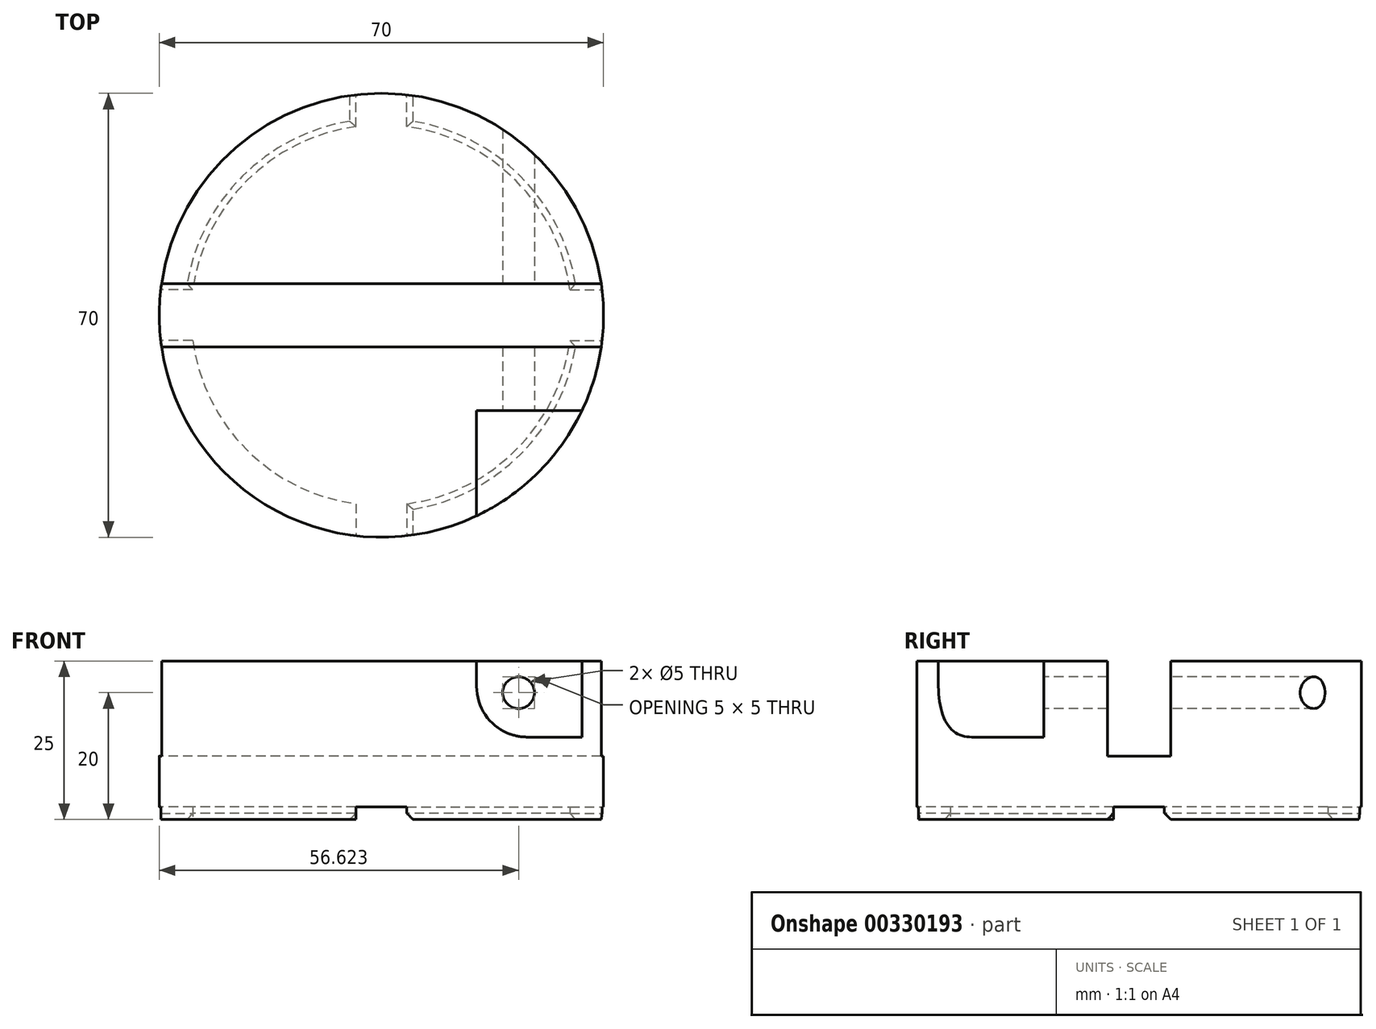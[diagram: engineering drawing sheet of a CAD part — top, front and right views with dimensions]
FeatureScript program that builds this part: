
annotation { "Feature Type Name" : "Feature", "Feature Type Description" : "" }
export const myFeature = defineFeature(function(context is Context, id is Id, definition is map)
    precondition{}
    {
        {
            var Q0;
            Q0=qCreatedBy(makeId("Top.planeOp"),FACE);
            var sketch = newSketch(context, id + "F0", { "sketchPlane" : qUnion([Q0])});
            skCircle(sketch, "E0", {"center": v(0, 0) * mm, "radius": 35 * mm});
            skSolve(sketch);
        }
        {
            var Q0;
            Q0=makeQuery(id+"F0.imprint","IMPRINT",FACE,{"disambiguationData":[TD([[makeQuery(id+"F0.imprint","IMPRINT",EDGE,{"derivedFrom":sQuery(id+"F0.wireOp",EDGE,"E0")}),1.0]])]});
            extrude(context, id + "F1", {"entities" : qUnion([Q0]), "depth" : 25 * mm});
        }
        {
            var Q0;
            Q0=makeQuery(id+"F1.opExtrude","CAP_FACE",FACE,{"disambiguationData":[OSD([sQuery(id+"F0.wireOp",EDGE,"E0")])],"isStart":false});
            var sketch = newSketch(context, id + "F2", { "sketchPlane" : qUnion([Q0])});
            skLineSegment(sketch, "E1.bottom", {"start": v(35, 5) * mm, "end": v(-35, 5) * mm});
            skLineSegment(sketch, "E1.top", {"start": v(35, -5) * mm, "end": v(-35, -5) * mm});
            skLineSegment(sketch, "E1.left", {"start": v(35, 5) * mm, "end": v(35, -5) * mm});
            skLineSegment(sketch, "E1.right", {"start": v(-35, 5) * mm, "end": v(-35, -5) * mm});
            skPoint(sketch, "E1.middle", {"position": v(0, 0) * mm});
            skSolve(sketch);
        }
        {
            var Q0;
            Q0 = qSketchRegion(id + "F2", true);
            extrude(context, id + "F3", {"entities" : qUnion([Q0]), "operationType" : NewBodyOperationType.REMOVE, "oppositeDirection" : true, "depth" : 15 * mm});
        }
        {
            var Q0;
            Q0=qCreatedBy(makeId("Front.planeOp"),FACE);
            cPlane(context, id + "F4", {"entities" : qUnion([Q0]), "cplaneType" : CPlaneType.OFFSET, "offset" : 15 * mm, "width" : 150 * mm, "height" : 150 * mm});
        }
        {
            var Q0;
            Q0=qCreatedBy(id+"F4.planeOp",FACE);
            var sketch = newSketch(context, id + "F5", { "sketchPlane" : qUnion([Q0])});
            skLineSegment(sketch, "E2.bottom", {"start": v(58, 33) * mm, "end": v(23, 33) * mm});
            skLineSegment(sketch, "E2.top", {"start": v(58, 13) * mm, "end": v(23, 13) * mm});
            skLineSegment(sketch, "E2.left", {"start": v(58, 33) * mm, "end": v(58, 13) * mm});
            skLineSegment(sketch, "E2.right", {"start": v(23, 33) * mm, "end": v(23, 13) * mm});
            skLineSegment(sketch, "E3.bottom", {"start": v(23, 33) * mm, "end": v(15, 33) * mm});
            skLineSegment(sketch, "E3.top", {"start": v(23, 21) * mm, "end": v(15, 21) * mm});
            skLineSegment(sketch, "E3.left", {"start": v(23, 33) * mm, "end": v(23, 21) * mm});
            skLineSegment(sketch, "E3.right", {"start": v(15, 33) * mm, "end": v(15, 21) * mm});
            skArc(sketch, "E4", {"start": v(15, 21) * mm, "mid": v(17.34, 15.34) * mm, "end": v(23, 13) * mm});
            skSolve(sketch);
        }
        {
            var Q0;
            Q0 = qSketchRegion(id + "F5", true);
            extrude(context, id + "F6", {"entities" : qUnion([Q0]), "operationType" : NewBodyOperationType.REMOVE, "depth" : 25 * mm});
        }
        {
            var Q0;
            Q0=makeQuery(id+"F6.boolean.opBoolean","COPY",FACE,{"derivedFrom":makeQuery(id+"F6.opExtrude","CAP_FACE",FACE,{"disambiguationData":[OSD([sQuery(id+"F5.wireOp",EDGE,"E2.bottom"),sQuery(id+"F5.wireOp",EDGE,"E2.top"),sQuery(id+"F5.wireOp",EDGE,"E2.left"),sQuery(id+"F5.wireOp",EDGE,"E3.bottom"),sQuery(id+"F5.wireOp",EDGE,"E3.right"),sQuery(id+"F5.wireOp",EDGE,"E4")])],"isStart":true})});
            var sketch = newSketch(context, id + "F7", { "sketchPlane" : qUnion([Q0])});
            skCircle(sketch, "E5", {"center": v(21.62, 20) * mm, "radius": 2.5 * mm});
            skSolve(sketch);
        }
        {
            var Q0;
            Q0=makeQuery(id+"F7.imprint","IMPRINT",FACE,{"disambiguationData":[TD([[makeQuery(id+"F7.imprint","IMPRINT",EDGE,{"derivedFrom":sQuery(id+"F7.wireOp",EDGE,"E5")}),1.0]])]});
            extrude(context, id + "F8", {"entities" : qUnion([Q0]), "operationType" : NewBodyOperationType.REMOVE, "oppositeDirection" : true, "depth" : 50 * mm});
        }
        {
            var Q0;
            Q0=makeQuery(id+"F1.opExtrude","CAP_FACE",FACE,{"disambiguationData":[OSD([sQuery(id+"F0.wireOp",EDGE,"E0")])],"isStart":true});
            var sketch = newSketch(context, id + "F9", { "sketchPlane" : qUnion([Q0])});
            skCircle(sketch, "E6", {"center": v(0, 0) * mm, "radius": 30 * mm});
            skLineSegment(sketch, "E7.bottom", {"start": v(-4, 29.73) * mm, "end": v(4, 29.73) * mm});
            skLineSegment(sketch, "E7.top", {"start": v(-4, 35.73) * mm, "end": v(4, 35.73) * mm});
            skLineSegment(sketch, "E7.left", {"start": v(-4, 29.73) * mm, "end": v(-4, 35.73) * mm});
            skLineSegment(sketch, "E7.right", {"start": v(4, 29.73) * mm, "end": v(4, 35.73) * mm});
            skLineSegment(sketch, "E8.1.0", {"start": v(-35.73, -4) * mm, "end": v(-35.73, 4) * mm});
            skLineSegment(sketch, "E8.1.1", {"start": v(-29.73, -4) * mm, "end": v(-35.73, -4) * mm});
            skLineSegment(sketch, "E8.1.2", {"start": v(-29.73, 4) * mm, "end": v(-35.73, 4) * mm});
            skLineSegment(sketch, "E8.1.3", {"start": v(-29.73, -4) * mm, "end": v(-29.73, 4) * mm});
            skLineSegment(sketch, "E8.2.0", {"start": v(4, -35.73) * mm, "end": v(-4, -35.73) * mm});
            skLineSegment(sketch, "E8.2.1", {"start": v(4, -29.73) * mm, "end": v(4, -35.73) * mm});
            skLineSegment(sketch, "E8.2.2", {"start": v(-4, -29.73) * mm, "end": v(-4, -35.73) * mm});
            skLineSegment(sketch, "E8.2.3", {"start": v(4, -29.73) * mm, "end": v(-4, -29.73) * mm});
            skLineSegment(sketch, "E8.3.0", {"start": v(35.73, 4) * mm, "end": v(35.73, -4) * mm});
            skLineSegment(sketch, "E8.3.1", {"start": v(29.73, 4) * mm, "end": v(35.73, 4) * mm});
            skLineSegment(sketch, "E8.3.2", {"start": v(29.73, -4) * mm, "end": v(35.73, -4) * mm});
            skLineSegment(sketch, "E8.3.3", {"start": v(29.73, 4) * mm, "end": v(29.73, -4) * mm});
            skSolve(sketch);
        }
        {
            var Q0;
            Q0 = qSketchRegion(id + "F9", true);
            extrude(context, id + "F10", {"entities" : qUnion([Q0]), "operationType" : NewBodyOperationType.REMOVE, "oppositeDirection" : true, "depth" : 2 * mm});
        }
        {
            var Q0;
            {var subQ0=sQuery(id+"F9.wireOp",EDGE,"E6");Q0=makeQuery(id+"F10.boolean.opBoolean","COPY",EDGE,{"derivedFrom":makeQuery(id+"F10.opExtrude","CAP_EDGE",EDGE,{"disambiguationData":[OSD([subQ0]),TDD([makeQuery(id+"F9.imprint","IMPRINT",EDGE,{"disambiguationData":[TD([[makeQuery(id+"F9.imprint","INTERSECT",VERTEX,{"derivedFrom":[subQ0,sQuery(id+"F9.wireOp",EDGE,"E7.bottom"),sQuery(id+"F9.wireOp",EDGE,"E7.left")]}),-1.0]])],"derivedFrom":subQ0})])],"isStart":true})});}
            var Q1;
            {var subQ0=sQuery(id+"F9.wireOp",EDGE,"E6");Q1=makeQuery(id+"F10.boolean.opBoolean","COPY",EDGE,{"derivedFrom":makeQuery(id+"F10.opExtrude","CAP_EDGE",EDGE,{"disambiguationData":[OSD([subQ0]),TDD([makeQuery(id+"F9.imprint","IMPRINT",EDGE,{"disambiguationData":[TD([[makeQuery(id+"F9.imprint","INTERSECT",VERTEX,{"derivedFrom":[subQ0,sQuery(id+"F9.wireOp",EDGE,"E7.bottom"),sQuery(id+"F9.wireOp",EDGE,"E7.right")]}),1.0]])],"derivedFrom":subQ0})])],"isStart":true})});}
            var Q2;
            {var subQ0=sQuery(id+"F9.wireOp",EDGE,"E6");Q2=makeQuery(id+"F10.boolean.opBoolean","COPY",EDGE,{"derivedFrom":makeQuery(id+"F10.opExtrude","CAP_EDGE",EDGE,{"disambiguationData":[OSD([subQ0]),TDD([makeQuery(id+"F9.imprint","IMPRINT",EDGE,{"disambiguationData":[TD([[makeQuery(id+"F9.imprint","INTERSECT",VERTEX,{"derivedFrom":[subQ0,sQuery(id+"F9.wireOp",EDGE,"E8.2.1"),sQuery(id+"F9.wireOp",EDGE,"E8.2.3")]}),-1.0]])],"derivedFrom":subQ0})])],"isStart":true})});}
            var Q3;
            {var subQ0=sQuery(id+"F9.wireOp",EDGE,"E6");Q3=makeQuery(id+"F10.boolean.opBoolean","COPY",EDGE,{"derivedFrom":makeQuery(id+"F10.opExtrude","CAP_EDGE",EDGE,{"disambiguationData":[OSD([subQ0]),TDD([makeQuery(id+"F9.imprint","IMPRINT",EDGE,{"disambiguationData":[TD([[makeQuery(id+"F9.imprint","INTERSECT",VERTEX,{"derivedFrom":[subQ0,sQuery(id+"F9.wireOp",EDGE,"E8.1.1"),sQuery(id+"F9.wireOp",EDGE,"E8.1.3")]}),-1.0]])],"derivedFrom":subQ0})])],"isStart":true})});}
            var Q4;
            Q4=makeQuery(id+"F10.boolean.opBoolean","COPY",EDGE,{"derivedFrom":makeQuery(id+"F10.opExtrude","CAP_EDGE",EDGE,{"disambiguationData":[OSD([sQuery(id+"F9.wireOp",EDGE,"E8.1.2")])],"isStart":true})});
            var Q5;
            Q5=makeQuery(id+"F10.boolean.opBoolean","COPY",EDGE,{"derivedFrom":makeQuery(id+"F10.opExtrude","CAP_EDGE",EDGE,{"disambiguationData":[OSD([sQuery(id+"F9.wireOp",EDGE,"E8.1.1")])],"isStart":true})});
            var Q6;
            Q6=makeQuery(id+"F10.boolean.opBoolean","COPY",EDGE,{"derivedFrom":makeQuery(id+"F10.opExtrude","CAP_EDGE",EDGE,{"disambiguationData":[OSD([sQuery(id+"F9.wireOp",EDGE,"E7.left")])],"isStart":true})});
            var Q7;
            Q7=makeQuery(id+"F10.boolean.opBoolean","COPY",EDGE,{"derivedFrom":makeQuery(id+"F10.opExtrude","CAP_EDGE",EDGE,{"disambiguationData":[OSD([sQuery(id+"F9.wireOp",EDGE,"E7.right")])],"isStart":true})});
            var Q8;
            Q8=makeQuery(id+"F10.boolean.opBoolean","COPY",EDGE,{"derivedFrom":makeQuery(id+"F10.opExtrude","CAP_EDGE",EDGE,{"disambiguationData":[OSD([sQuery(id+"F9.wireOp",EDGE,"E8.3.1")])],"isStart":true})});
            var Q9;
            Q9=makeQuery(id+"F10.boolean.opBoolean","COPY",EDGE,{"derivedFrom":makeQuery(id+"F10.opExtrude","CAP_EDGE",EDGE,{"disambiguationData":[OSD([sQuery(id+"F9.wireOp",EDGE,"E8.3.2")])],"isStart":true})});
            var Q10;
            Q10=makeQuery(id+"F10.boolean.opBoolean","COPY",EDGE,{"derivedFrom":makeQuery(id+"F10.opExtrude","CAP_EDGE",EDGE,{"disambiguationData":[OSD([sQuery(id+"F9.wireOp",EDGE,"E8.2.1")])],"isStart":true})});
            var Q11;
            Q11=makeQuery(id+"F10.boolean.opBoolean","COPY",EDGE,{"derivedFrom":makeQuery(id+"F10.opExtrude","CAP_EDGE",EDGE,{"disambiguationData":[OSD([sQuery(id+"F9.wireOp",EDGE,"E8.2.2")])],"isStart":true})});
            chamfer(context, id + "F11", {"entities" : qUnion([Q0, Q1, Q2, Q3, Q4, Q5, Q6, Q7, Q8, Q9, Q10, Q11]), "width" : 1 * mm, "tangentPropagation" : true});
        }
    });
